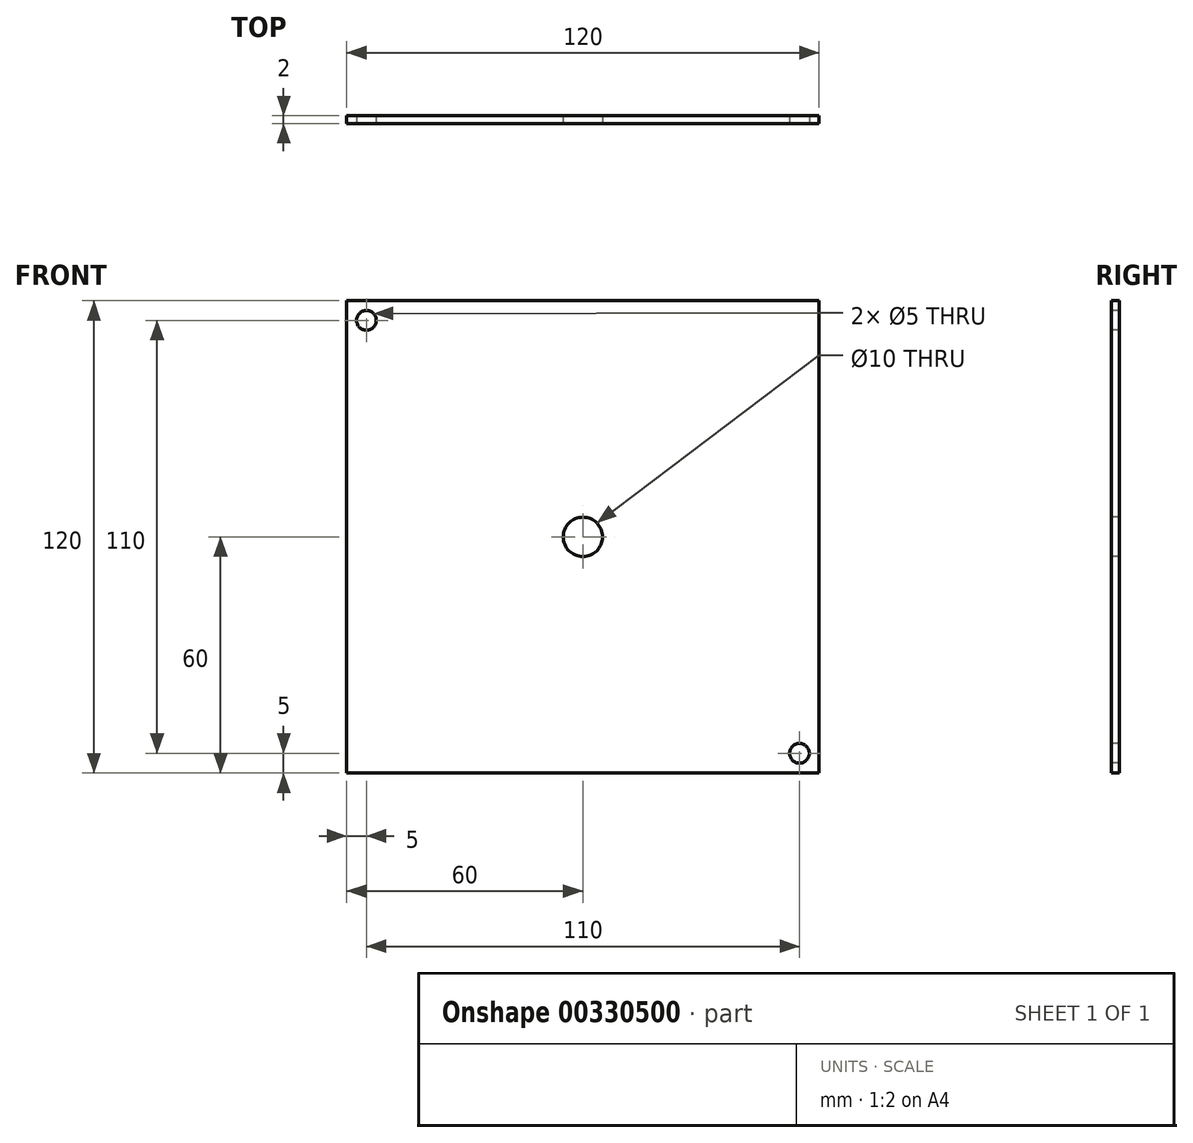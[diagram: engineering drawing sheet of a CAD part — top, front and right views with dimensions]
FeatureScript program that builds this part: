
annotation { "Feature Type Name" : "Feature", "Feature Type Description" : "" }
export const myFeature = defineFeature(function(context is Context, id is Id, definition is map)
    precondition{}
    {
        {
            var Q0;
            Q0=qCreatedBy(makeId("Front.planeOp"),FACE);
            var sketch = newSketch(context, id + "F0", { "sketchPlane" : qUnion([Q0])});
            skLineSegment(sketch, "E0.bottom", {"start": v(60, -60) * mm, "end": v(-60, -60) * mm});
            skLineSegment(sketch, "E0.top", {"start": v(60, 60) * mm, "end": v(-60, 60) * mm});
            skLineSegment(sketch, "E0.left", {"start": v(60, -60) * mm, "end": v(60, 60) * mm});
            skLineSegment(sketch, "E0.right", {"start": v(-60, -60) * mm, "end": v(-60, 60) * mm});
            skPoint(sketch, "E0.middle", {"position": v(0, 0) * mm});
            skSolve(sketch);
        }
        {
            var Q0;
            Q0=makeQuery(id+"F0.imprint","IMPRINT",FACE,{"disambiguationData":[TD([[makeQuery(id+"F0.imprint","IMPRINT",EDGE,{"derivedFrom":sQuery(id+"F0.wireOp",EDGE,"E0.bottom")}),-1.0]])]});
            extrude(context, id + "F1", {"entities" : qUnion([Q0]), "depth" : 2 * mm});
        }
        {
            var Q0;
            Q0=makeQuery(id+"F1.opExtrude","CAP_FACE",FACE,{"disambiguationData":[OSD([sQuery(id+"F0.wireOp",EDGE,"E0.bottom"),sQuery(id+"F0.wireOp",EDGE,"E0.top"),sQuery(id+"F0.wireOp",EDGE,"E0.left"),sQuery(id+"F0.wireOp",EDGE,"E0.right")])],"isStart":false});
            var sketch = newSketch(context, id + "F2", { "sketchPlane" : qUnion([Q0])});
            skCircle(sketch, "E1", {"center": v(-55, 55) * mm, "radius": 2.5 * mm});
            skCircle(sketch, "E2", {"center": v(55, -55) * mm, "radius": 2.5 * mm});
            skSolve(sketch);
        }
        {
            var Q0;
            Q0=makeQuery(id+"F2.imprint","IMPRINT",FACE,{"disambiguationData":[TD([[makeQuery(id+"F2.imprint","IMPRINT",EDGE,{"derivedFrom":sQuery(id+"F2.wireOp",EDGE,"E1")}),1.0]])]});
            var Q1;
            Q1=makeQuery(id+"F2.imprint","IMPRINT",FACE,{"disambiguationData":[TD([[makeQuery(id+"F2.imprint","IMPRINT",EDGE,{"derivedFrom":sQuery(id+"F2.wireOp",EDGE,"E2")}),1.0]])]});
            extrude(context, id + "F3", {"entities" : qUnion([Q0, Q1]), "operationType" : NewBodyOperationType.REMOVE, "endBound" : BoundingType.THROUGH_ALL, "oppositeDirection" : true, "depth" : 25 * mm});
        }
        {
            var Q0;
            Q0=makeQuery(id+"F1.opExtrude","CAP_FACE",FACE,{"disambiguationData":[OSD([sQuery(id+"F0.wireOp",EDGE,"E0.bottom"),sQuery(id+"F0.wireOp",EDGE,"E0.top"),sQuery(id+"F0.wireOp",EDGE,"E0.left"),sQuery(id+"F0.wireOp",EDGE,"E0.right")])],"isStart":false});
            var sketch = newSketch(context, id + "F4", { "sketchPlane" : qUnion([Q0])});
            skCircle(sketch, "E3", {"center": v(0, 0) * mm, "radius": 5 * mm});
            skSolve(sketch);
        }
        {
            var Q0;
            Q0=makeQuery(id+"F4.imprint","IMPRINT",FACE,{"disambiguationData":[TD([[makeQuery(id+"F4.imprint","IMPRINT",EDGE,{"derivedFrom":sQuery(id+"F4.wireOp",EDGE,"E3")}),1.0]])]});
            extrude(context, id + "F5", {"entities" : qUnion([Q0]), "operationType" : NewBodyOperationType.REMOVE, "endBound" : BoundingType.THROUGH_ALL, "oppositeDirection" : true, "depth" : 25 * mm});
        }
    });
